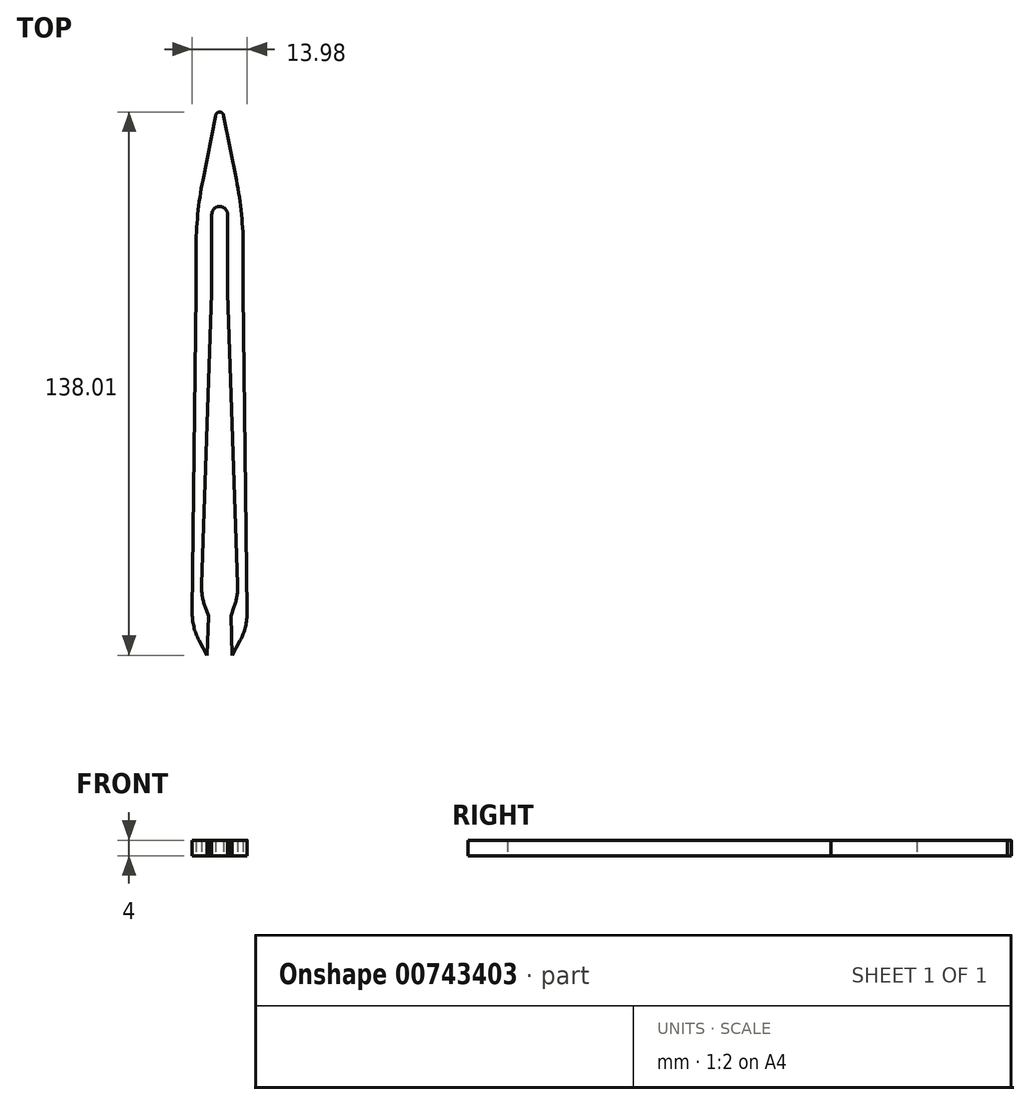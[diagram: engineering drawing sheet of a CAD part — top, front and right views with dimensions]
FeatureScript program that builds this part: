
annotation { "Feature Type Name" : "Feature", "Feature Type Description" : "" }
export const myFeature = defineFeature(function(context is Context, id is Id, definition is map)
    precondition{}
    {
        {
            var Q0;
            Q0=qCreatedBy(makeId("Top.planeOp"),FACE);
            var sketch = newSketch(context, id + "F0", { "sketchPlane" : qUnion([Q0])});
            skLineSegment(sketch, "E0", {"start": v(0, -54.84) * mm, "end": v(0, -64.84) * mm});
            skLineSegment(sketch, "E1", {"start": v(-2, -49.84) * mm, "end": v(-2, 27.16) * mm});
            skLineSegment(sketch, "E2", {"start": v(-2, 27.16) * mm, "end": v(-6, 27.16) * mm});
            skLineSegment(sketch, "E3", {"start": v(-6, 27.16) * mm, "end": v(-4.07, -57.84) * mm});
            skLineSegment(sketch, "E4", {"start": v(-4.07, -57.84) * mm, "end": v(0, -64.84) * mm});
            skLineSegment(sketch, "E5", {"start": v(-2, -49.84) * mm, "end": v(0, -54.84) * mm});
            skSolve(sketch);
        }
        {
            var Q0;
            Q0=makeQuery(id+"F0.imprint","IMPRINT",FACE,{"disambiguationData":[TD([[makeQuery(id+"F0.imprint","IMPRINT",EDGE,{"derivedFrom":sQuery(id+"F0.wireOp",EDGE,"E0")}),-1.0]])]});
            extrude(context, id + "F1", {"entities" : qUnion([Q0]), "depth" : 4 * mm, "offsetDistance" : 25 * mm});
        }
        {
            var Q0;
            Q0=makeQuery(id+"F1.opExtrude","SWEPT_EDGE",EDGE,{"disambiguationData":[OSD([sQuery(id+"F0.wireOp",EDGE,"E3"),sQuery(id+"F0.wireOp",EDGE,"E4")])]});
            var Q1;
            Q1=makeQuery(id+"F1.opExtrude","SWEPT_EDGE",EDGE,{"disambiguationData":[OSD([sQuery(id+"F0.wireOp",EDGE,"E1"),sQuery(id+"F0.wireOp",EDGE,"E5")])]});
            fillet(context, id + "F2", {"entities" : qUnion([Q0, Q1]), "radius" : 15 * mm, "tangentPropagation" : true, "allowEdgeOverflow" : false});
        }
        {
            var Q0;
            Q0=makeQuery(id+"F1.opExtrude","SWEPT_BODY",BODY,{"disambiguationData":[OSD([sQuery(id+"F0.wireOp",EDGE,"E0"),sQuery(id+"F0.wireOp",EDGE,"E1"),sQuery(id+"F0.wireOp",EDGE,"E2"),sQuery(id+"F0.wireOp",EDGE,"E3"),sQuery(id+"F0.wireOp",EDGE,"E4"),sQuery(id+"F0.wireOp",EDGE,"E5")])]});
            var Q1;
            Q1=makeQuery(id+"F1.opExtrude","SWEPT_EDGE",EDGE,{"disambiguationData":[OSD([sQuery(id+"F0.wireOp",EDGE,"E1"),sQuery(id+"F0.wireOp",EDGE,"E2")])]});
            transform(context, id + "F3", {"entities" : qUnion([Q0]), "transformType" : TransformType.ROTATION, "transformAxis" : qUnion([Q1]), "angle" : 2 * degree, "makeCopy" : false});
        }
        {
            var Q0;
            Q0=makeQuery(id+"F1.opExtrude","CAP_FACE",FACE,{"disambiguationData":[OSD([sQuery(id+"F0.wireOp",EDGE,"E0"),sQuery(id+"F0.wireOp",EDGE,"E1"),sQuery(id+"F0.wireOp",EDGE,"E2"),sQuery(id+"F0.wireOp",EDGE,"E3"),sQuery(id+"F0.wireOp",EDGE,"E4"),sQuery(id+"F0.wireOp",EDGE,"E5")])],"isStart":true});
            var sketch = newSketch(context, id + "F4", { "sketchPlane" : qUnion([Q0])});
            skLineSegment(sketch, "E6", {"start": v(-2, -27.16) * mm, "end": v(-2, -47.16) * mm});
            skArc(sketch, "E7", {"start": v(-2, -47.16) * mm, "mid": v(-1.41, -48.58) * mm, "end": v(0, -49.16) * mm});
            skLineSegment(sketch, "E8", {"start": v(-6, -27.3) * mm, "end": v(-6, -47.16) * mm});
            skLineSegment(sketch, "E9", {"start": v(-6, -47.16) * mm, "end": v(-1, -72.16) * mm});
            skArc(sketch, "E10", {"start": v(-1, -72.16) * mm, "mid": v(-0.7, -72.87) * mm, "end": v(0, -73.16) * mm});
            skLineSegment(sketch, "E11", {"start": v(0, -73.16) * mm, "end": v(0, -49.16) * mm});
            skSolve(sketch);
        }
        {
            var Q0;
            Q0=makeQuery(id+"F4.imprint","IMPRINT",FACE,{"disambiguationData":[TD([[makeQuery(id+"F4.imprint","IMPRINT",EDGE,{"derivedFrom":sQuery(id+"F4.wireOp",EDGE,"E6")}),-1.0]])]});
            extrude(context, id + "F5", {"entities" : qUnion([Q0]), "operationType" : NewBodyOperationType.ADD, "oppositeDirection" : true, "depth" : 4 * mm, "offsetDistance" : 25 * mm});
        }
        {
            var Q0;
            Q0=makeQuery(id+"F1.opExtrude","SWEPT_BODY",BODY,{"disambiguationData":[OSD([sQuery(id+"F0.wireOp",EDGE,"E0"),sQuery(id+"F0.wireOp",EDGE,"E1"),sQuery(id+"F0.wireOp",EDGE,"E2"),sQuery(id+"F0.wireOp",EDGE,"E3"),sQuery(id+"F0.wireOp",EDGE,"E4"),sQuery(id+"F0.wireOp",EDGE,"E5")])]});
            var Q1;
            Q1=qCreatedBy(makeId("Right.planeOp"),FACE);
            mirror(context, id + "F6", {"operationType" : NewBodyOperationType.ADD, "entities" : qUnion([Q0]), "mirrorPlane" : qUnion([Q1])});
        }
        {
            var Q0;
            Q0=makeQuery(id+"F5.opExtrude","SWEPT_EDGE",EDGE,{"disambiguationData":[OSD([sQuery(id+"F4.wireOp",EDGE,"E8"),sQuery(id+"F4.wireOp",EDGE,"E9")])]});
            var Q1;
            Q1=makeQuery(id+"F6.opPattern","COPY",EDGE,{"derivedFrom":makeQuery(id+"F5.opExtrude","SWEPT_EDGE",EDGE,{"disambiguationData":[OSD([sQuery(id+"F4.wireOp",EDGE,"E8"),sQuery(id+"F4.wireOp",EDGE,"E9")])]}),"instanceName":"1"});
            fillet(context, id + "F7", {"entities" : qUnion([Q0, Q1]), "radius" : 90 * mm, "tangentPropagation" : true, "allowEdgeOverflow" : false});
        }
    });
